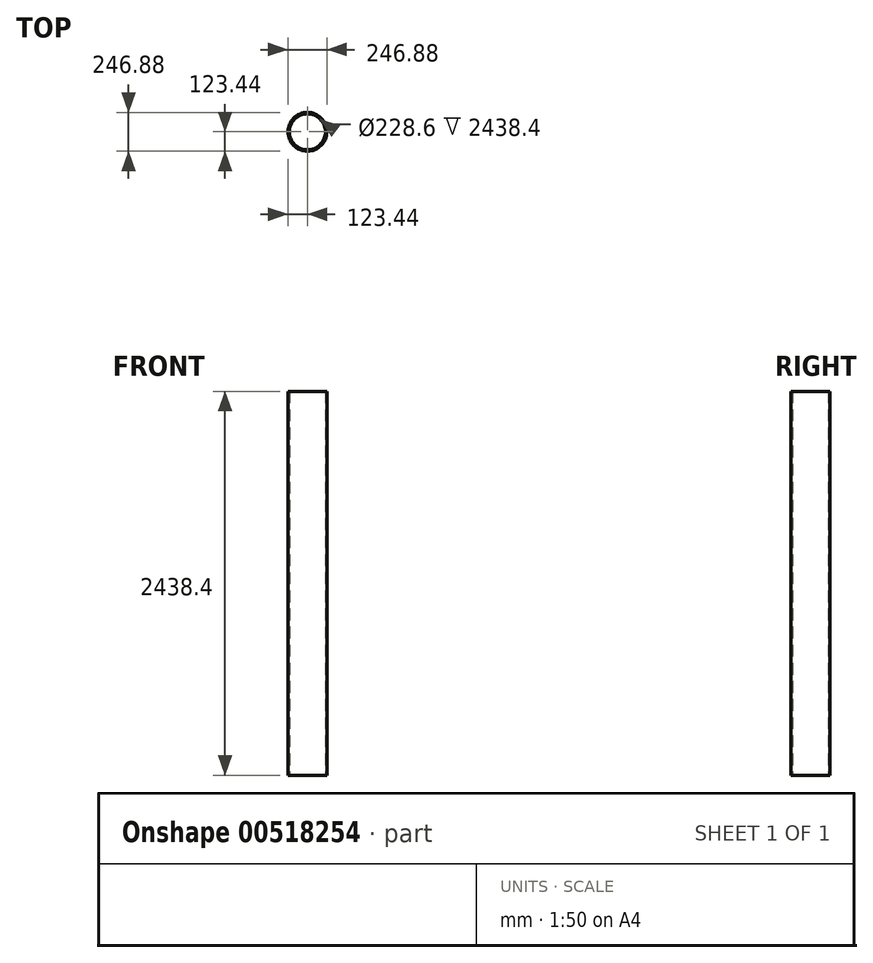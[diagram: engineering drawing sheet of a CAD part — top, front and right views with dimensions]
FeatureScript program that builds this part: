
annotation { "Feature Type Name" : "Feature", "Feature Type Description" : "" }
export const myFeature = defineFeature(function(context is Context, id is Id, definition is map)
    precondition{}
    {
        {
            var Q0;
            Q0=qCreatedBy(makeId("Top.planeOp"),FACE);
            var sketch = newSketch(context, id + "F0", { "sketchPlane" : qUnion([Q0])});
            skCircle(sketch, "E0", {"center": v(0, 0) * mm, "radius": 123.44 * mm});
            skCircle(sketch, "E1", {"center": v(0, 0) * mm, "radius": 114.3 * mm});
            skSolve(sketch);
        }
        {
            var Q0;
            Q0 = qSketchRegion(id + "F0", true);
            extrude(context, id + "F1", {"entities" : qUnion([Q0]), "depth" : 2438.4 * mm, "offsetDistance" : 30.48 * mm});
        }
    });
